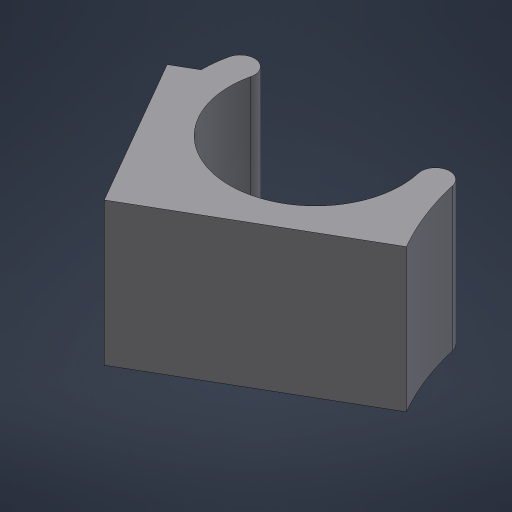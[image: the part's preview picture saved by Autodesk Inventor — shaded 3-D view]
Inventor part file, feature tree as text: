
AUTODESK INVENTOR PART (.ipt)
format: ipt  version: 2023.5 (Build 275446000, 446)  size: 154,624 bytes
history: native  units: mm
features: extrude x1, sketch x1
ambient origin geometry x8: Origin, YZ Plane, XZ Plane, XY Plane, X Axis, Y Axis, Z Axis, Center Point
bodies: Volumenkörper1 (feature_tree)
feature tree (2):
  extrude  "Extrusion1"  Depth=15.0mm
  sketch  "Skizze1"  dims[d0=18.0mm d1=3.0mm d2=2.0mm d4=18.0mm d5=13.0mm d6=120.0deg d7=15.0mm d8=0.0mm]
